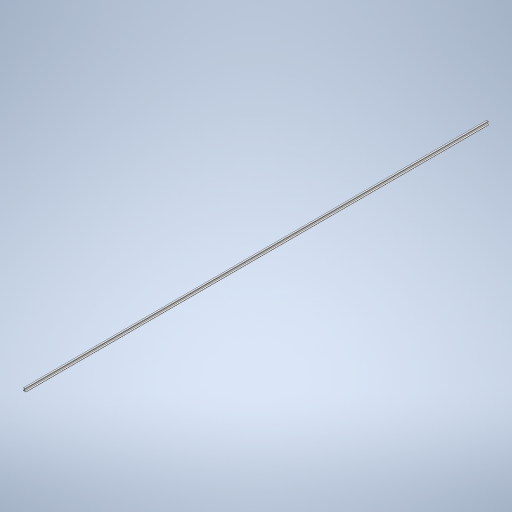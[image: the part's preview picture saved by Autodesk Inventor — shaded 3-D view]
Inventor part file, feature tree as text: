
AUTODESK INVENTOR PART (.ipt)
format: ipt  version: 2023 (Build 270158030, 158C)  size: 262,656 bytes
history: native  units: in
note: dims shown in document units (in); Inventor stores cm internally (conversion verified against a paired STEP export)
features: extrude x1, sketch x1
ambient origin geometry x8: Origin, YZ Plane, XZ Plane, XY Plane, X Axis, Y Axis, Z Axis, Center Point
bodies: Solid1 (feature_tree)
feature tree (2):
  extrude  "Extrusion1"  Depth=24.0in
  sketch  "Sketch1"  dims[d3=0.026in d4=0.0104in d5=1.1475in d6=0.0833in d7=0.0417in d9=0.0893in d10=0.01in d11=24.0in d12=0.0in]
